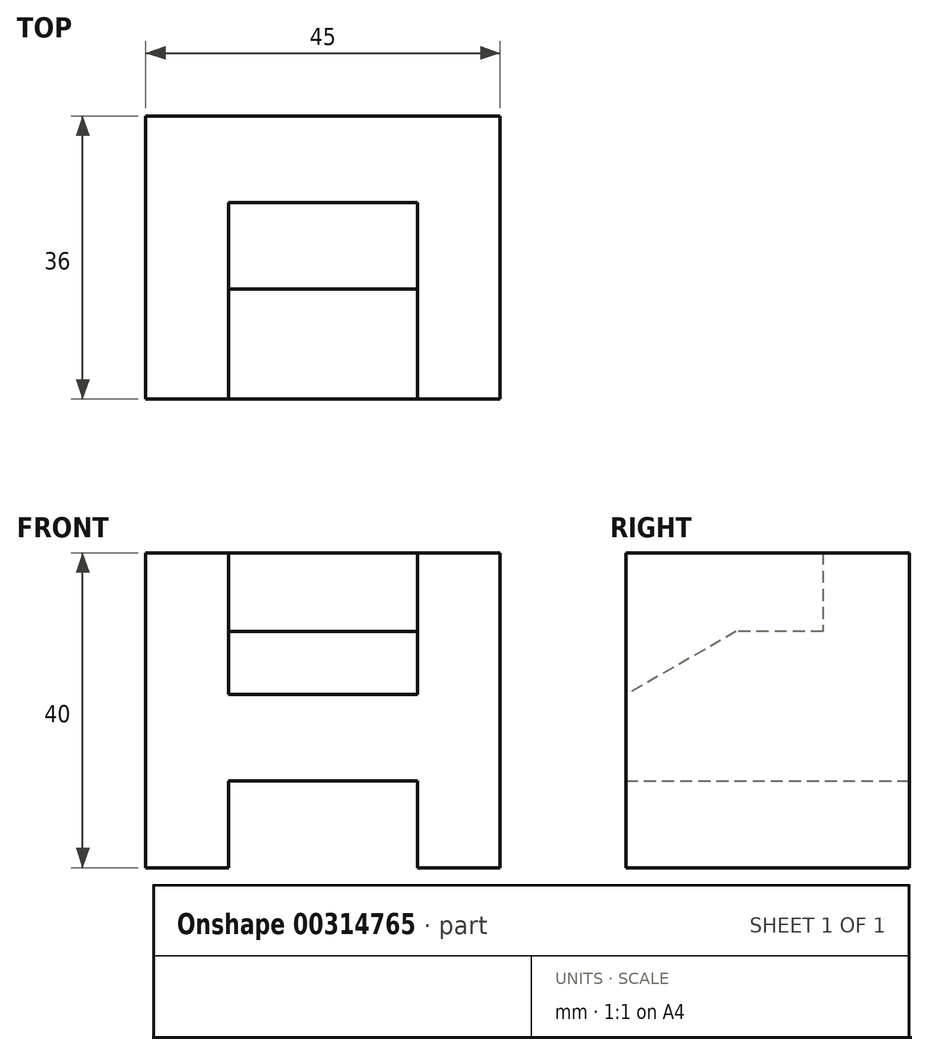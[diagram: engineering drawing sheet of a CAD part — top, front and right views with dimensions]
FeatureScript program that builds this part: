
annotation { "Feature Type Name" : "Feature", "Feature Type Description" : "" }
export const myFeature = defineFeature(function(context is Context, id is Id, definition is map)
    precondition{}
    {
        {
            var Q0;
            Q0=qCreatedBy(makeId("Right.planeOp"),FACE);
            var sketch = newSketch(context, id + "F0", { "sketchPlane" : qUnion([Q0])});
            skLineSegment(sketch, "E0.bottom", {"start": v(0, 0) * mm, "end": v(36, 0) * mm});
            skLineSegment(sketch, "E0.top", {"start": v(0, 40) * mm, "end": v(36, 40) * mm});
            skLineSegment(sketch, "E0.left", {"start": v(0, 0) * mm, "end": v(0, 40) * mm});
            skLineSegment(sketch, "E0.right", {"start": v(36, 0) * mm, "end": v(36, 40) * mm});
            skLineSegment(sketch, "E1", {"start": v(0, 11) * mm, "end": v(36, 11) * mm});
            skLineSegment(sketch, "E2", {"start": v(25, 40) * mm, "end": v(25, 30) * mm});
            skLineSegment(sketch, "E3", {"start": v(25, 30) * mm, "end": v(14, 30) * mm});
            skLineSegment(sketch, "E4", {"start": v(14, 30) * mm, "end": v(0, 22) * mm});
            skSolve(sketch);
        }
        {
            var Q0;
            Q0 = qSketchRegion(id + "F0", true);
            extrude(context, id + "F1", {"entities" : qUnion([Q0]), "depth" : 45 * mm, "symmetric" : true});
        }
        {
            var Q0;
            {var subQ0=sQuery(id+"F0.wireOp",EDGE,"E0.bottom");Q0=makeQuery(id+"F0.imprint","IMPRINT",FACE,{"disambiguationData":[TD([[makeQuery(id+"F0.imprint","IMPRINT",EDGE,{"derivedFrom":subQ0}),1.0]])]});}
            extrude(context, id + "F2", {"entities" : qUnion([Q0]), "operationType" : NewBodyOperationType.REMOVE, "oppositeDirection" : true, "depth" : 24 * mm, "symmetric" : true});
        }
        {
            var Q0;
            {var subQ0=sQuery(id+"F0.wireOp",EDGE,"E2");Q0=makeQuery(id+"F0.imprint","IMPRINT",FACE,{"disambiguationData":[TD([[makeQuery(id+"F0.imprint","IMPRINT",EDGE,{"derivedFrom":subQ0}),-1.0]])]});}
            extrude(context, id + "F3", {"entities" : qUnion([Q0]), "operationType" : NewBodyOperationType.REMOVE, "oppositeDirection" : true, "depth" : 24 * mm, "symmetric" : true});
        }
    });
